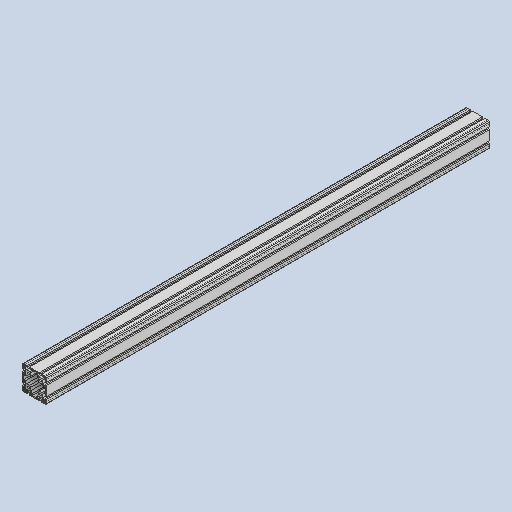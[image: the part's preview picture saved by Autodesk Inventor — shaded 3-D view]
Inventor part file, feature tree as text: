
AUTODESK INVENTOR PART (.ipt)
format: ipt  version: 2022 (Build 260153000, 153)  size: 210,944 bytes
history: native  units: in
note: dims shown in document units (in); Inventor stores cm internally (conversion verified against a paired STEP export)
features: extrude x1
ambient origin geometry x8: Origin, YZ Plane, XZ Plane, XY Plane, X Axis, Y Axis, Z Axis, Center Point
bodies: Solid1 (feature_tree)
feature tree (1):
  extrude  "Extrusion2"  [1 undecoded]
note: 1 required parameter value undecoded (feature->parameter linkage not recoverable at this tier; creation-order binding heuristic only, values carry confidence <= 0.55)
